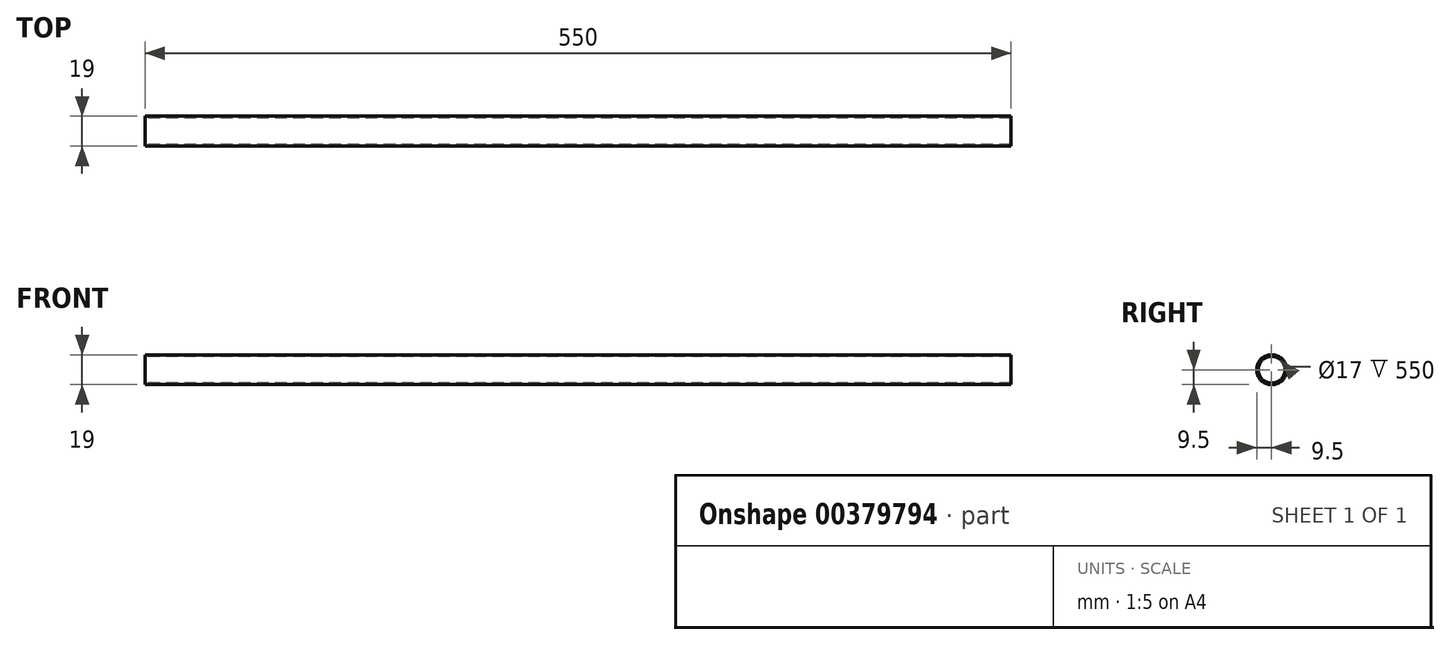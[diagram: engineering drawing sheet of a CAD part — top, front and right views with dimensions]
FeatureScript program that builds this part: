
annotation { "Feature Type Name" : "Feature", "Feature Type Description" : "" }
export const myFeature = defineFeature(function(context is Context, id is Id, definition is map)
    precondition{}
    {
        {
            var Q0;
            Q0=qCreatedBy(makeId("Right.planeOp"),FACE);
            var sketch = newSketch(context, id + "F0", { "sketchPlane" : qUnion([Q0])});
            skCircle(sketch, "E0", {"center": v(0, 0) * mm, "radius": 9.5 * mm});
            skCircle(sketch, "E1", {"center": v(0, 0) * mm, "radius": 8.5 * mm});
            skSolve(sketch);
        }
        {
            var Q0;
            Q0 = qSketchRegion(id + "F0", true);
            extrude(context, id + "F1", {"entities" : qUnion([Q0]), "depth" : 550 * mm, "offsetDistance" : 25 * mm});
        }
    });
